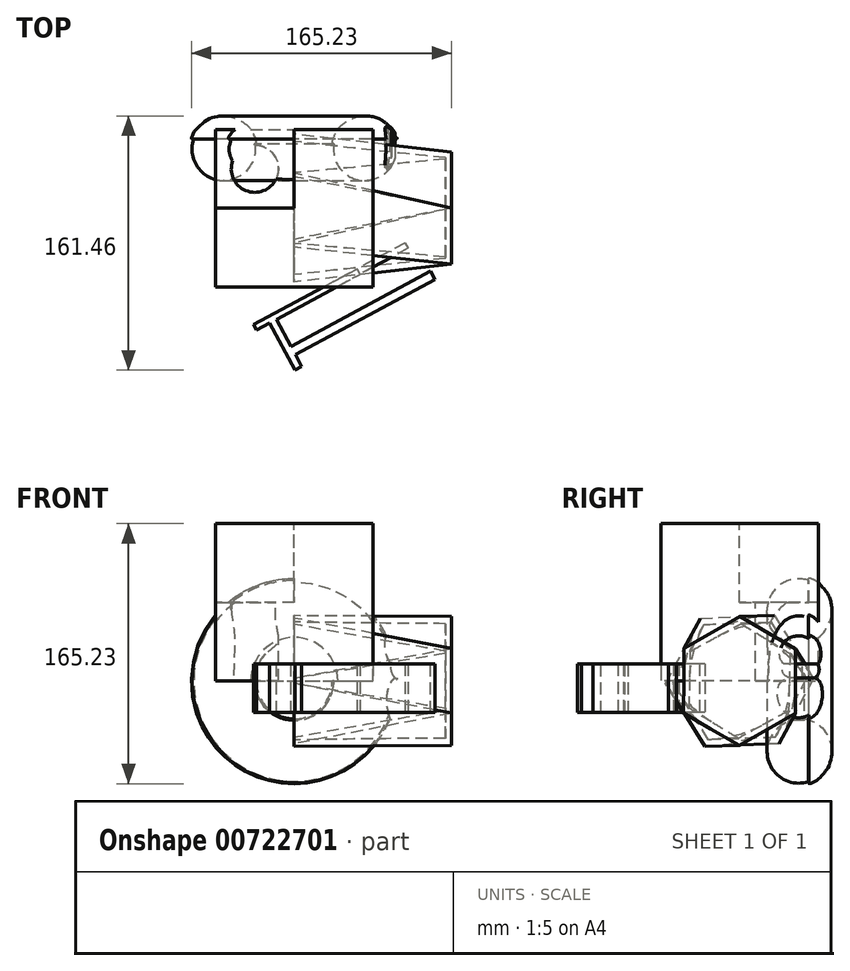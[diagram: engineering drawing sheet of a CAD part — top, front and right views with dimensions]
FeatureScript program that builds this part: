
annotation { "Feature Type Name" : "Feature", "Feature Type Description" : "" }
export const myFeature = defineFeature(function(context is Context, id is Id, definition is map)
    precondition{}
    {
        {
            var Q0;
            Q0=qCreatedBy(makeId("Top.planeOp"),FACE);
            var sketch = newSketch(context, id + "F0", { "sketchPlane" : qUnion([Q0])});
            skLineSegment(sketch, "E0.bottom", {"start": v(-50, 50) * mm, "end": v(50, 50) * mm});
            skLineSegment(sketch, "E0.top", {"start": v(-50, -50) * mm, "end": v(50, -50) * mm});
            skLineSegment(sketch, "E0.left", {"start": v(-50, 50) * mm, "end": v(-50, -50) * mm});
            skLineSegment(sketch, "E0.right", {"start": v(50, 50) * mm, "end": v(50, -50) * mm});
            skPoint(sketch, "E0.middle", {"position": v(0, 0) * mm});
            skSolve(sketch);
        }
        {
            var Q0;
            Q0=makeQuery(id+"F0.imprint","IMPRINT",FACE,{"disambiguationData":[TD([[makeQuery(id+"F0.imprint","IMPRINT",EDGE,{"derivedFrom":sQuery(id+"F0.wireOp",EDGE,"E0.bottom")}),-1.0]])]});
            extrude(context, id + "F1", {"entities" : qUnion([Q0]), "depth" : 100 * mm, "offsetDistance" : 25 * mm});
        }
        {
            var Q0;
            Q0=makeQuery(id+"F1.opExtrude","CAP_FACE",FACE,{"disambiguationData":[OSD([sQuery(id+"F0.wireOp",EDGE,"E0.bottom"),sQuery(id+"F0.wireOp",EDGE,"E0.top"),sQuery(id+"F0.wireOp",EDGE,"E0.left"),sQuery(id+"F0.wireOp",EDGE,"E0.right")])],"isStart":false});
            var sketch = newSketch(context, id + "F2", { "sketchPlane" : qUnion([Q0])});
            skLineSegment(sketch, "E1.bottom", {"start": v(0, 0) * mm, "end": v(-59.62, 0) * mm});
            skLineSegment(sketch, "E1.top", {"start": v(0, 56.08) * mm, "end": v(-59.62, 56.08) * mm});
            skLineSegment(sketch, "E1.left", {"start": v(0, 0) * mm, "end": v(0, 56.08) * mm});
            skLineSegment(sketch, "E1.right", {"start": v(-59.62, 0) * mm, "end": v(-59.62, 56.08) * mm});
            skSolve(sketch);
        }
        {
            var Q0;
            {var subQ0=sQuery(id+"F2.wireOp",EDGE,"E1.left");var subQ1=sQuery(id+"F2.wireOp",EDGE,"E1.bottom");var subQ2=makeQuery(id+"F2.imprint","INTERSECT",VERTEX,{"derivedFrom":[subQ1,subQ0]});Q0=makeQuery(id+"F2.imprint","IMPRINT",FACE,{"disambiguationData":[TD([[makeQuery(id+"F2.imprint","IMPRINT",EDGE,{"disambiguationData":[TD([[subQ2,-1.0]])],"derivedFrom":subQ1}),-1.0]])]});}
            extrude(context, id + "F3", {"entities" : qUnion([Q0]), "operationType" : NewBodyOperationType.REMOVE, "oppositeDirection" : true, "depth" : 50 * mm, "offsetDistance" : 25 * mm});
        }
        {
            var Q0;
            Q0=makeQuery(id+"F3.boolean.opBoolean","COPY",FACE,{"derivedFrom":makeQuery(id+"F3.opExtrude","CAP_FACE",FACE,{"disambiguationData":[OSD([sQuery(id+"F0.wireOp",EDGE,"E0.bottom"),sQuery(id+"F0.wireOp",EDGE,"E0.left"),sQuery(id+"F2.wireOp",EDGE,"E1.bottom"),sQuery(id+"F2.wireOp",EDGE,"E1.left")])],"isStart":false})});
            var sketch = newSketch(context, id + "F4", { "sketchPlane" : qUnion([Q0])});
            skCircle(sketch, "E2", {"center": v(-25, 25) * mm, "radius": 15 * mm});
            skPoint(sketch, "E2.centerSnap0", {"position": v(-25, 50) * mm});
            skPoint(sketch, "E2.centerSnap1", {"position": v(-50, 25) * mm});
            skSolve(sketch);
        }
        {
            var Q0;
            Q0=makeQuery(id+"F4.imprint","IMPRINT",FACE,{"disambiguationData":[TD([[makeQuery(id+"F4.imprint","IMPRINT",EDGE,{"derivedFrom":sQuery(id+"F4.wireOp",EDGE,"E2")}),1.0]])]});
            extrude(context, id + "F5", {"entities" : qUnion([Q0]), "operationType" : NewBodyOperationType.REMOVE, "oppositeDirection" : true, "depth" : 50 * mm, "offsetDistance" : 25 * mm});
        }
        {
            var Q0;
            Q0=qCreatedBy(makeId("Top.planeOp"),FACE);
            var sketch = newSketch(context, id + "F6", { "sketchPlane" : qUnion([Q0])});
            skLineSegment(sketch, "E3", {"start": v(0, 78.42) * mm, "end": v(0, -66.02) * mm});
            skCircle(sketch, "E4", {"center": v(44.9, 37.44) * mm, "radius": 20 * mm});
            skPoint(sketch, "E4.first.point", {"position": v(25.18, 40.78) * mm});
            skPoint(sketch, "E4.second.point", {"position": v(40.29, 17.98) * mm});
            skPoint(sketch, "E4.third.point", {"position": v(49.5, 17.98) * mm});
            skFitSpline(sketch, "E5", {"points": [v(25.18, 40.78) * mm, v(24.29, 42.55) * mm, v(28.02, 50.48) * mm, v(34.64, 55.7) * mm, v(43.08, 58.52) * mm, v(54.33, 56.53) * mm, v(59.6, 52.62) * mm, v(63.4, 48.76) * mm, v(65.23, 44) * mm, v(63.8, 43.96) * mm, v(25.18, 40.78) * mm]});
            skSolve(sketch);
        }
        {
            var Q0;
            Q0=makeQuery(id+"F6.imprint","IMPRINT",FACE,{"disambiguationData":[TD([[makeQuery(id+"F6.imprint","IMPRINT",EDGE,{"derivedFrom":sQuery(id+"F6.wireOp",EDGE,"E4")}),1.0]])]});
            var Q1;
            Q1=sQuery(id+"F6.wireOp",EDGE,"E3");
            revolve(context, id + "F7", {"surfaceOperationType" : NewSurfaceOperationType.NEW, "entities" : qUnion([Q0]), "axis" : qUnion([Q1]), "revolveType" : RevolveType.FULL});
        }
        {
            var Q0;
            Q0 = qSketchRegion(id + "F6", true);
            var Q1;
            Q1=sQuery(id+"F6.wireOp",EDGE,"E3");
            revolve(context, id + "F8", {"operationType" : NewBodyOperationType.ADD, "surfaceOperationType" : NewSurfaceOperationType.NEW, "entities" : qUnion([Q0]), "axis" : qUnion([Q1]), "revolveType" : RevolveType.FULL});
        }
        {
            var Q0;
            Q0=qCreatedBy(makeId("Front.planeOp"),FACE);
            var sketch = newSketch(context, id + "F9", { "sketchPlane" : qUnion([Q0])});
            skEllipse(sketch, "E6", {"center": v(67.46, 23.23) * mm, "majorRadius": 9.9 * mm, "minorRadius": 15.26 * mm, "majorAxis": v(-1, 0)});
            skCircle(sketch, "E7", {"center": v(70.7, 8.32) * mm, "radius": 9.2 * mm});
            skPoint(sketch, "E7.first.point", {"position": v(78.84, 4) * mm});
            skPoint(sketch, "E7.second.point", {"position": v(61.82, 10.7) * mm});
            skPoint(sketch, "E7.third.point", {"position": v(61.67, 6.62) * mm});
            skCircle(sketch, "E8", {"center": v(76.8, -1.37) * mm, "radius": 12.06 * mm});
            skPoint(sketch, "E8.first.point", {"position": v(68.77, -10.36) * mm});
            skPoint(sketch, "E8.second.point", {"position": v(76.8, 10.7) * mm});
            skPoint(sketch, "E8.third.point", {"position": v(84.44, 7.97) * mm});
            skPoint(sketch, "E8.third.point.positionSnap0", {"position": v(67.46, 7.97) * mm});
            skEllipse(sketch, "E9", {"center": v(69.14, -16.7) * mm, "majorRadius": 19.67 * mm, "minorRadius": 9.91 * mm, "majorAxis": v(-0.16, 0.99)});
            skSolve(sketch);
        }
        {
            var Q0;
            Q0 = qSketchRegion(id + "F9", true);
            extrude(context, id + "F10", {"entities" : qUnion([Q0]), "operationType" : NewBodyOperationType.REMOVE, "oppositeDirection" : true, "depth" : 60 * mm, "offsetDistance" : 25 * mm});
        }
        {
            var Q0;
            Q0=qCreatedBy(makeId("Right.planeOp"),FACE);
            cPlane(context, id + "F11", {"entities" : qUnion([Q0]), "cplaneType" : CPlaneType.OFFSET, "offset" : 100 * mm, "width" : 150 * mm, "height" : 150 * mm});
        }
        {
            var Q0;
            Q0=qCreatedBy(id+"F11.planeOp",FACE);
            var sketch = newSketch(context, id + "F12", { "sketchPlane" : qUnion([Q0])});
            skCircle(sketch, "E10.cCircle", {"center": v(0, 0) * mm, "radius": 35.51 * mm, "construction": true});
            skLineSegment(sketch, "E10.0", {"start": v(35.47, -20.57) * mm, "end": v(-0.08, -41) * mm});
            skLineSegment(sketch, "E10.1", {"start": v(-0.08, -41) * mm, "end": v(-35.55, -20.43) * mm});
            skLineSegment(sketch, "E10.2", {"start": v(-35.55, -20.43) * mm, "end": v(-35.47, 20.57) * mm});
            skLineSegment(sketch, "E10.3", {"start": v(-35.47, 20.57) * mm, "end": v(0.08, 41) * mm});
            skLineSegment(sketch, "E10.4", {"start": v(0.08, 41) * mm, "end": v(35.55, 20.43) * mm});
            skLineSegment(sketch, "E10.5", {"start": v(35.55, 20.43) * mm, "end": v(35.47, -20.57) * mm});
            skPoint(sketch, "E10.0.midPoint", {"position": v(17.7, -30.79) * mm});
            skSolve(sketch);
        }
        {
            var Q0;
            Q0=qCreatedBy(makeId("Right.planeOp"),FACE);
            var sketch = newSketch(context, id + "F13", { "sketchPlane" : qUnion([Q0])});
            skCircle(sketch, "E11.cCircle", {"center": v(0, 0) * mm, "radius": 40.7 * mm, "construction": true});
            skLineSegment(sketch, "E11.0", {"start": v(-46.97, -1.61) * mm, "end": v(-24.88, 39.87) * mm});
            skLineSegment(sketch, "E11.1", {"start": v(-24.88, 39.87) * mm, "end": v(22.09, 41.48) * mm});
            skLineSegment(sketch, "E11.2", {"start": v(22.09, 41.48) * mm, "end": v(46.97, 1.61) * mm});
            skLineSegment(sketch, "E11.3", {"start": v(46.97, 1.61) * mm, "end": v(24.88, -39.87) * mm});
            skLineSegment(sketch, "E11.4", {"start": v(24.88, -39.87) * mm, "end": v(-22.09, -41.48) * mm});
            skLineSegment(sketch, "E11.5", {"start": v(-22.09, -41.48) * mm, "end": v(-46.97, -1.61) * mm});
            skPoint(sketch, "E11.0.midPoint", {"position": v(-35.92, 19.13) * mm});
            skSolve(sketch);
        }
        {
            var Q0;
            Q0=makeQuery(id+"F12.imprint","IMPRINT",FACE,{"disambiguationData":[TD([[makeQuery(id+"F12.imprint","IMPRINT",EDGE,{"derivedFrom":sQuery(id+"F12.wireOp",EDGE,"E10.0")}),-1.0]])]});
            var Q1;
            Q1=makeQuery(id+"F13.imprint","IMPRINT",FACE,{"disambiguationData":[TD([[makeQuery(id+"F13.imprint","IMPRINT",EDGE,{"derivedFrom":sQuery(id+"F13.wireOp",EDGE,"E11.0")}),-1.0]])]});
            loft(context, id + "F14", {"sheetProfilesArray" : [{ "sheetProfileEntities" : qUnion([Q0]) }, { "sheetProfileEntities" : qUnion([Q1]) }]});
        }
        {
            var Q0;
            Q0=makeQuery(id+"F14.opLoft","CAP_FACE",FACE,{"disambiguationData":[OSD([makeQuery(id+"F13.imprint","IMPRINT",FACE,{"disambiguationData":[TD([[makeQuery(id+"F13.imprint","IMPRINT",EDGE,{"derivedFrom":sQuery(id+"F13.wireOp",EDGE,"E11.0")}),-1.0]])]})])],"isStart":true});
            shell(context, id + "F15", {"entities" : qUnion([Q0]), "thickness" : 4 * mm});
        }
        {
            var Q0;
            Q0=qCreatedBy(makeId("Top.planeOp"),FACE);
            var sketch = newSketch(context, id + "F16", { "sketchPlane" : qUnion([Q0])});
            skLineSegment(sketch, "E12", {"start": v(-35.32, -72.7) * mm, "end": v(37.1, -33.63) * mm});
            skSolve(sketch);
        }
        {
            var Q0;
            Q0=sQuery(id+"F16.wireOp",EDGE,"E12");
            var Q1;
            Q1=sQuery(id+"F16.wireOp",VERTEX,"E12.end");
            cPlane(context, id + "F17", {"entities" : qUnion([Q0, Q1]), "cplaneType" : CPlaneType.CURVE_POINT, "offset" : 25 * mm, "width" : 150 * mm, "height" : 150 * mm});
        }
        {
            var Q0;
            Q0=qCreatedBy(id+"F17.planeOp",FACE);
            var sketch = newSketch(context, id + "F18", { "sketchPlane" : qUnion([Q0])});
            skLineSegment(sketch, "E13.bottom", {"start": v(-52.85, 10.86) * mm, "end": v(-56.79, 10.86) * mm});
            skLineSegment(sketch, "E13.top", {"start": v(-52.85, -20.02) * mm, "end": v(-56.79, -20.02) * mm});
            skLineSegment(sketch, "E13.left", {"start": v(-52.85, 10.86) * mm, "end": v(-52.85, -20.02) * mm});
            skLineSegment(sketch, "E13.right", {"start": v(-56.79, 10.86) * mm, "end": v(-56.79, -20.02) * mm});
            skSolve(sketch);
        }
        {
            var Q0;
            Q0=makeQuery(id+"F18.imprint","IMPRINT",FACE,{"disambiguationData":[TD([[makeQuery(id+"F18.imprint","IMPRINT",EDGE,{"derivedFrom":sQuery(id+"F18.wireOp",EDGE,"E13.bottom")}),1.0]])]});
            extrude(context, id + "F19", {"entities" : qUnion([Q0]), "oppositeDirection" : true, "depth" : 74.4 * mm, "offsetDistance" : 25 * mm});
        }
        {
            var Q0;
            Q0=makeQuery(id+"F19.opExtrude","SWEPT_FACE",FACE,{"disambiguationData":[OSD([sQuery(id+"F18.wireOp",EDGE,"E13.right")])]});
            var sketch = newSketch(context, id + "F20", { "sketchPlane" : qUnion([Q0])});
            skLineSegment(sketch, "E14.bottom", {"start": v(-48.38, -20.02) * mm, "end": v(-43.6, -20.02) * mm});
            skLineSegment(sketch, "E14.top", {"start": v(-48.38, 10.86) * mm, "end": v(-43.6, 10.86) * mm});
            skLineSegment(sketch, "E14.left", {"start": v(-48.38, -20.02) * mm, "end": v(-48.38, 10.86) * mm});
            skLineSegment(sketch, "E14.right", {"start": v(-43.6, -20.02) * mm, "end": v(-43.6, 10.86) * mm});
            skSolve(sketch);
        }
        {
            var Q0;
            Q0=makeQuery(id+"F20.imprint","IMPRINT",FACE,{"disambiguationData":[TD([[makeQuery(id+"F20.imprint","IMPRINT",EDGE,{"derivedFrom":sQuery(id+"F20.wireOp",EDGE,"E14.bottom")}),1.0]])]});
            extrude(context, id + "F21", {"entities" : qUnion([Q0]), "operationType" : NewBodyOperationType.ADD, "depth" : 34 * mm, "offsetDistance" : 25 * mm});
        }
        {
            var Q0;
            Q0=makeQuery(id+"F21.opExtrude","SWEPT_FACE",FACE,{"disambiguationData":[OSD([sQuery(id+"F20.wireOp",EDGE,"E14.right")])]});
            var sketch = newSketch(context, id + "F22", { "sketchPlane" : qUnion([Q0])});
            skLineSegment(sketch, "E15.bottom", {"start": v(-82.34, -20.02) * mm, "end": v(-76.42, -20.02) * mm});
            skLineSegment(sketch, "E15.top", {"start": v(-82.34, 10.86) * mm, "end": v(-76.42, 10.86) * mm});
            skLineSegment(sketch, "E15.left", {"start": v(-82.34, -20.02) * mm, "end": v(-82.34, 10.86) * mm});
            skLineSegment(sketch, "E15.right", {"start": v(-76.42, -20.02) * mm, "end": v(-76.42, 10.86) * mm});
            skSolve(sketch);
        }
        {
            var Q0;
            Q0=makeQuery(id+"F22.imprint","IMPRINT",FACE,{"disambiguationData":[TD([[makeQuery(id+"F22.imprint","IMPRINT",EDGE,{"derivedFrom":sQuery(id+"F22.wireOp",EDGE,"E15.bottom")}),1.0]])]});
            extrude(context, id + "F23", {"entities" : qUnion([Q0]), "operationType" : NewBodyOperationType.ADD, "depth" : 100.7 * mm, "offsetDistance" : 25 * mm});
        }
        {
            var Q0;
            Q0=makeQuery(id+"F19.opExtrude","CAP_FACE",FACE,{"disambiguationData":[OSD([sQuery(id+"F18.wireOp",EDGE,"E13.bottom"),sQuery(id+"F18.wireOp",EDGE,"E13.top"),sQuery(id+"F18.wireOp",EDGE,"E13.left"),sQuery(id+"F18.wireOp",EDGE,"E13.right")])],"isStart":true});
            extrude(context, id + "F24", {"entities" : qUnion([Q0]), "depth" : 34.8 * mm, "offsetDistance" : 25 * mm});
        }
    });
